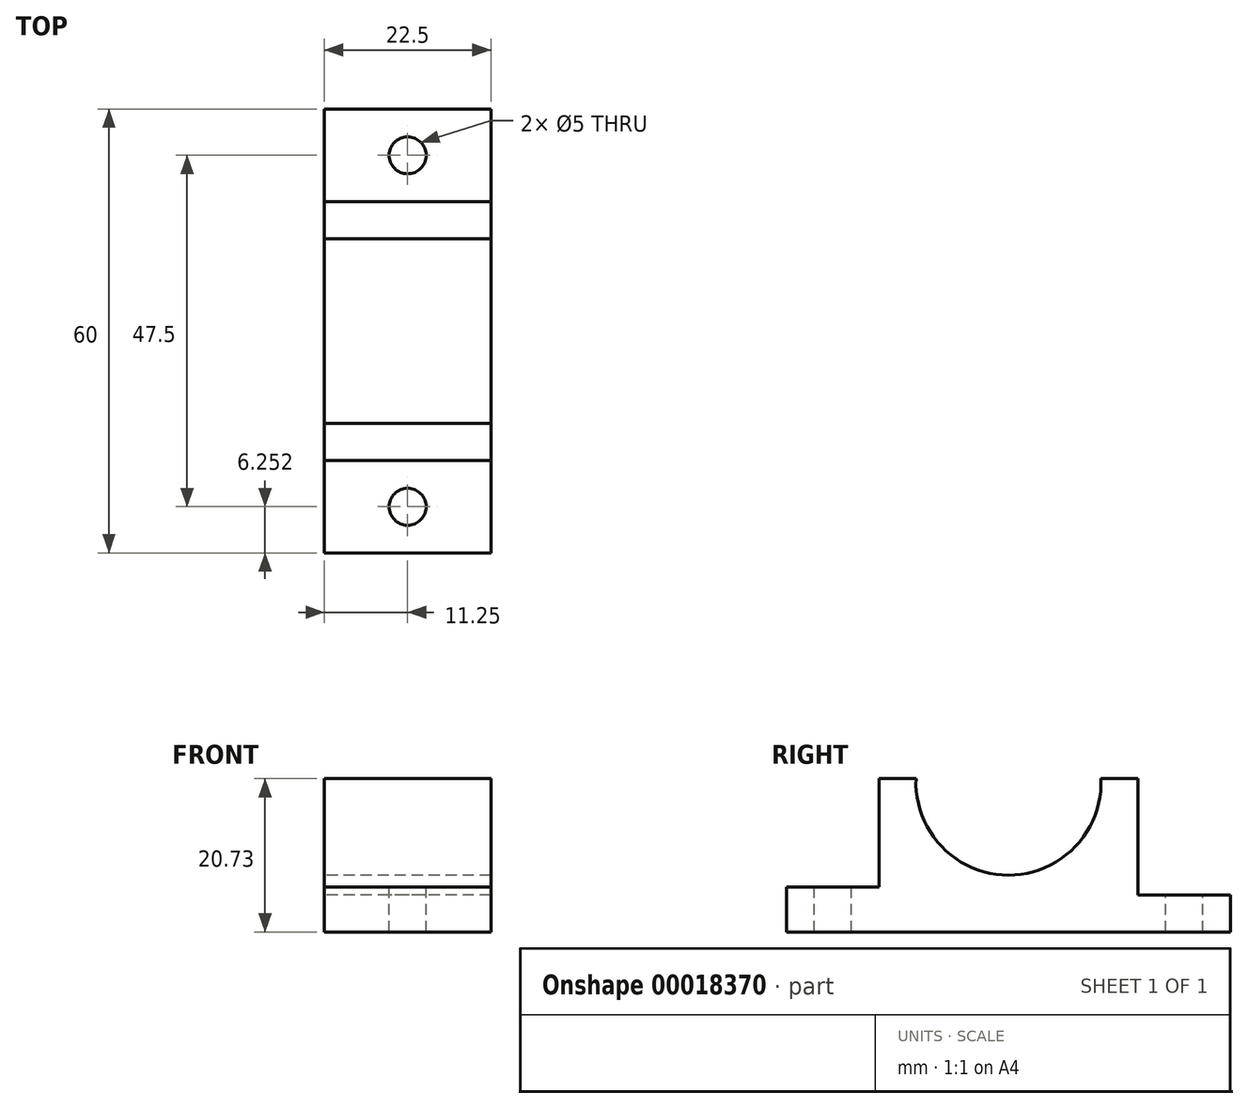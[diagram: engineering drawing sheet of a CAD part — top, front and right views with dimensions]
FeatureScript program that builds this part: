
annotation { "Feature Type Name" : "Feature", "Feature Type Description" : "" }
export const myFeature = defineFeature(function(context is Context, id is Id, definition is map)
    precondition{}
    {
        {
            var Q0;
            Q0=qCreatedBy(makeId("Right.planeOp"),FACE);
            var sketch = newSketch(context, id + "F0", { "sketchPlane" : qUnion([Q0])});
            skLineSegment(sketch, "E0", {"start": v(-43.26, 27.17) * mm, "end": v(16.74, 27.17) * mm});
            skLineSegment(sketch, "E1", {"start": v(-43.26, 27.17) * mm, "end": v(-43.26, 33.21) * mm});
            skLineSegment(sketch, "E2", {"start": v(16.74, 27.17) * mm, "end": v(16.74, 32.17) * mm});
            skLineSegment(sketch, "E3", {"start": v(-43.26, 33.21) * mm, "end": v(-30.76, 33.21) * mm});
            skLineSegment(sketch, "E4", {"start": v(16.74, 32.17) * mm, "end": v(4.24, 32.17) * mm});
            skLineSegment(sketch, "E5", {"start": v(-30.76, 33.21) * mm, "end": v(-30.76, 47.9) * mm});
            skLineSegment(sketch, "E6", {"start": v(4.24, 32.17) * mm, "end": v(4.24, 47.9) * mm});
            skLineSegment(sketch, "E7", {"start": v(-30.76, 47.9) * mm, "end": v(-25.76, 47.9) * mm});
            skLineSegment(sketch, "E8", {"start": v(-0.76, 47.9) * mm, "end": v(4.24, 47.9) * mm});
            skArc(sketch, "E9", {"start": v(-25.76, 47.9) * mm, "mid": v(-13.26, 34.86) * mm, "end": v(-0.76, 47.9) * mm});
            skSolve(sketch);
        }
        {
            var Q0;
            Q0=makeQuery(id+"F0.imprint","IMPRINT",FACE,{"disambiguationData":[TD([[makeQuery(id+"F0.imprint","IMPRINT",EDGE,{"derivedFrom":sQuery(id+"F0.wireOp",EDGE,"E0")}),1.0]])]});
            extrude(context, id + "F1", {"entities" : qUnion([Q0]), "depth" : 22.5 * mm});
        }
        {
            var Q0;
            Q0=makeQuery(id+"F1.opExtrude","SWEPT_FACE",FACE,{"disambiguationData":[OSD([sQuery(id+"F0.wireOp",EDGE,"E3")])]});
            var sketch = newSketch(context, id + "F2", { "sketchPlane" : qUnion([Q0])});
            skCircle(sketch, "E10", {"center": v(11.25, -37) * mm, "radius": 2.5 * mm});
            skSolve(sketch);
        }
        {
            var Q0;
            Q0=makeQuery(id+"F2.imprint","IMPRINT",FACE,{"disambiguationData":[TD([[makeQuery(id+"F2.imprint","IMPRINT",EDGE,{"derivedFrom":sQuery(id+"F2.wireOp",EDGE,"E10")}),1.0]])]});
            extrude(context, id + "F3", {"entities" : qUnion([Q0]), "operationType" : NewBodyOperationType.REMOVE, "endBound" : BoundingType.THROUGH_ALL, "oppositeDirection" : true, "depth" : 25 * mm});
        }
        {
            var Q0;
            Q0=makeQuery(id+"F1.opExtrude","SWEPT_FACE",FACE,{"disambiguationData":[OSD([sQuery(id+"F0.wireOp",EDGE,"E4")])]});
            var sketch = newSketch(context, id + "F4", { "sketchPlane" : qUnion([Q0])});
            skCircle(sketch, "E11", {"center": v(11.25, 10.5) * mm, "radius": 2.5 * mm});
            skSolve(sketch);
        }
        {
            var Q0;
            Q0=makeQuery(id+"F4.imprint","IMPRINT",FACE,{"disambiguationData":[TD([[makeQuery(id+"F4.imprint","IMPRINT",EDGE,{"derivedFrom":sQuery(id+"F4.wireOp",EDGE,"E11")}),1.0]])]});
            extrude(context, id + "F5", {"entities" : qUnion([Q0]), "operationType" : NewBodyOperationType.REMOVE, "endBound" : BoundingType.THROUGH_ALL, "oppositeDirection" : true, "depth" : 25 * mm});
        }
    });
